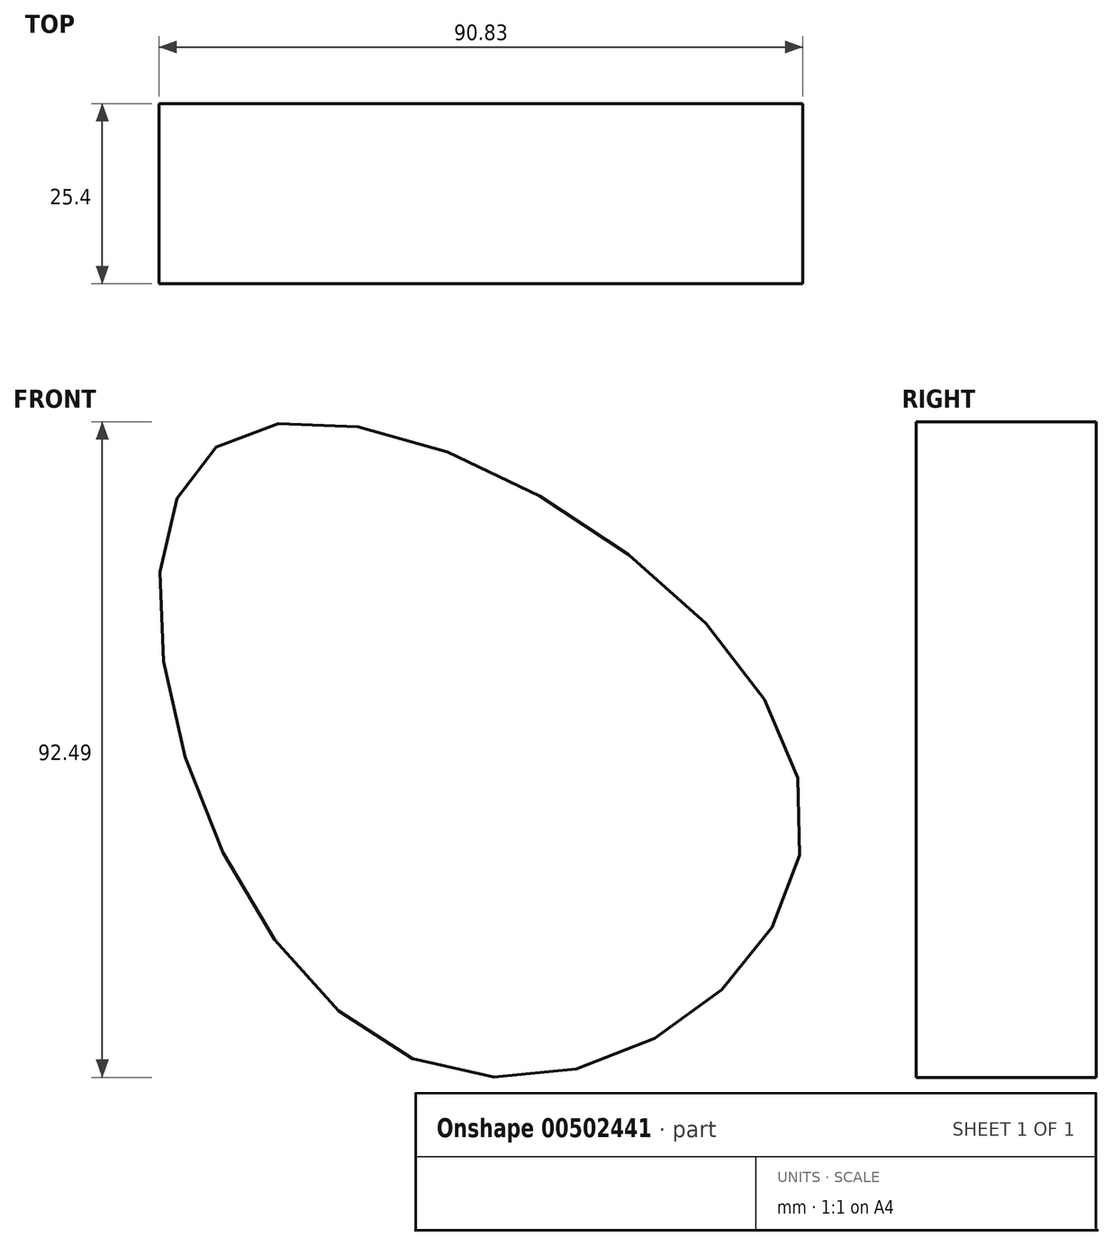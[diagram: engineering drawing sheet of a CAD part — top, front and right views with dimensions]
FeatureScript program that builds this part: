
annotation { "Feature Type Name" : "Feature", "Feature Type Description" : "" }
export const myFeature = defineFeature(function(context is Context, id is Id, definition is map)
    precondition{}
    {
        {
            var Q0;
            Q0=qCreatedBy(makeId("Front.planeOp"),FACE);
            var sketch = newSketch(context, id + "F0", { "sketchPlane" : qUnion([Q0])});
            skFitSpline(sketch, "E0", {"points": [v(-56.5, 61.2) * mm, v(25.99, 12.23) * mm, v(-29.2, -24.93) * mm, v(-56.5, 61.2) * mm]});
            skSolve(sketch);
        }
        {
            var Q0;
            Q0 = qSketchRegion(id + "F0", true);
            extrude(context, id + "F1", {"entities" : qUnion([Q0]), "depth" : 25.4 * mm});
        }
    });
